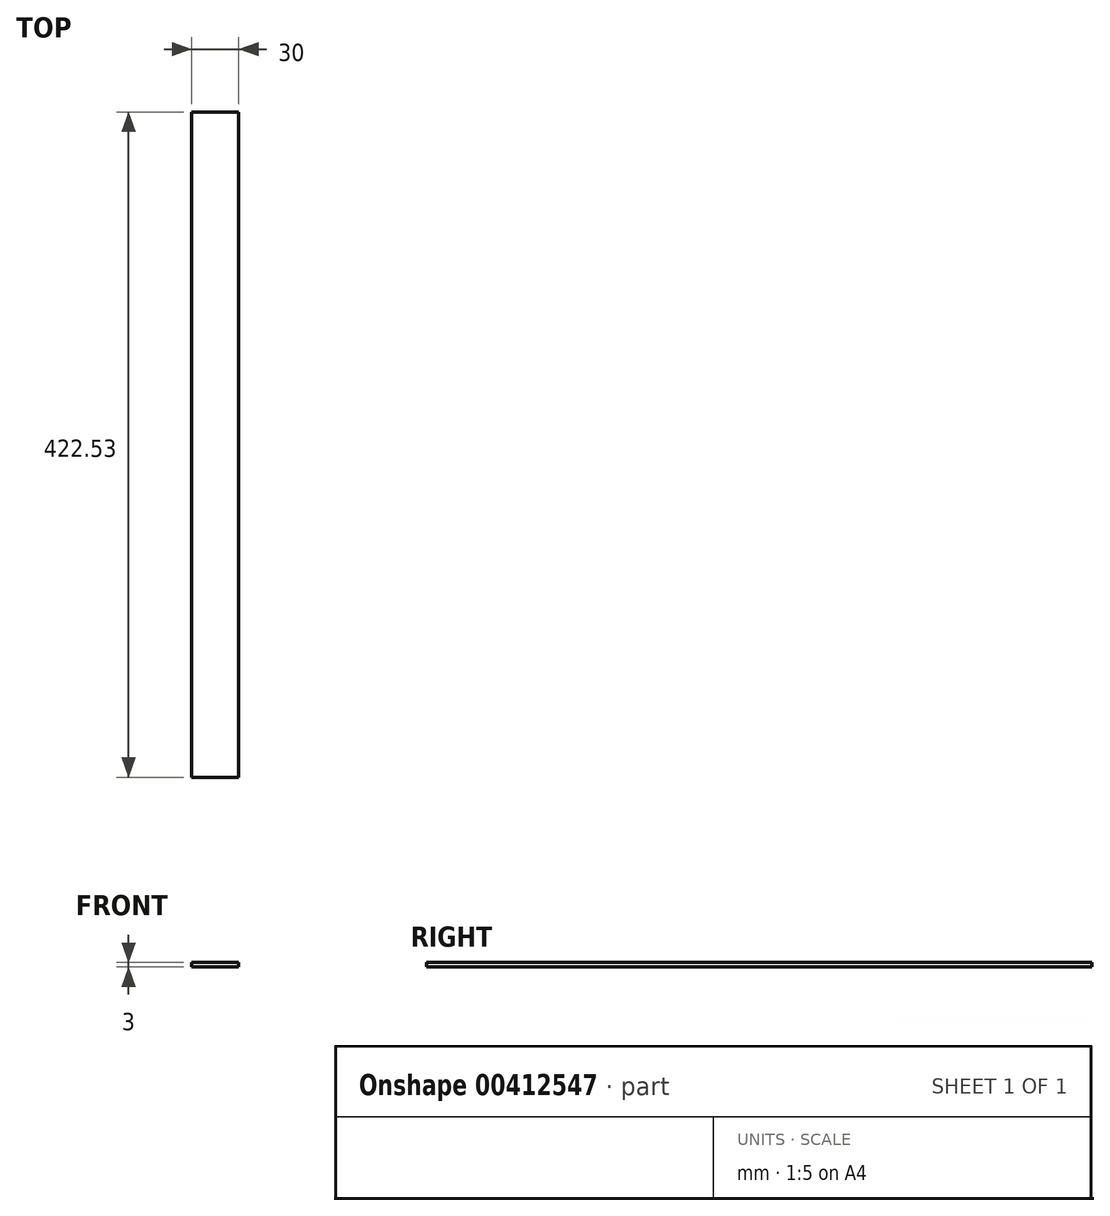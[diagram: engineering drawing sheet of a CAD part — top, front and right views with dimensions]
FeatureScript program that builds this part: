
annotation { "Feature Type Name" : "Feature", "Feature Type Description" : "" }
export const myFeature = defineFeature(function(context is Context, id is Id, definition is map)
    precondition{}
    {
        {
            var Q0;
            Q0=qCreatedBy(makeId("Top.planeOp"),FACE);
            var sketch = newSketch(context, id + "F0", { "sketchPlane" : qUnion([Q0])});
            skLineSegment(sketch, "E0.bottom", {"start": v(-59.13, 378.03) * mm, "end": v(-29.13, 378.03) * mm});
            skLineSegment(sketch, "E0.top", {"start": v(-59.13, -44.5) * mm, "end": v(-29.13, -44.5) * mm});
            skLineSegment(sketch, "E0.left", {"start": v(-59.13, 378.03) * mm, "end": v(-59.13, -44.5) * mm});
            skLineSegment(sketch, "E0.right", {"start": v(-29.13, 378.03) * mm, "end": v(-29.13, -44.5) * mm});
            skSolve(sketch);
        }
        {
            var Q0;
            Q0 = qSketchRegion(id + "F0", true);
            extrude(context, id + "F1", {"entities" : qUnion([Q0]), "depth" : 3 * mm});
        }
    });
